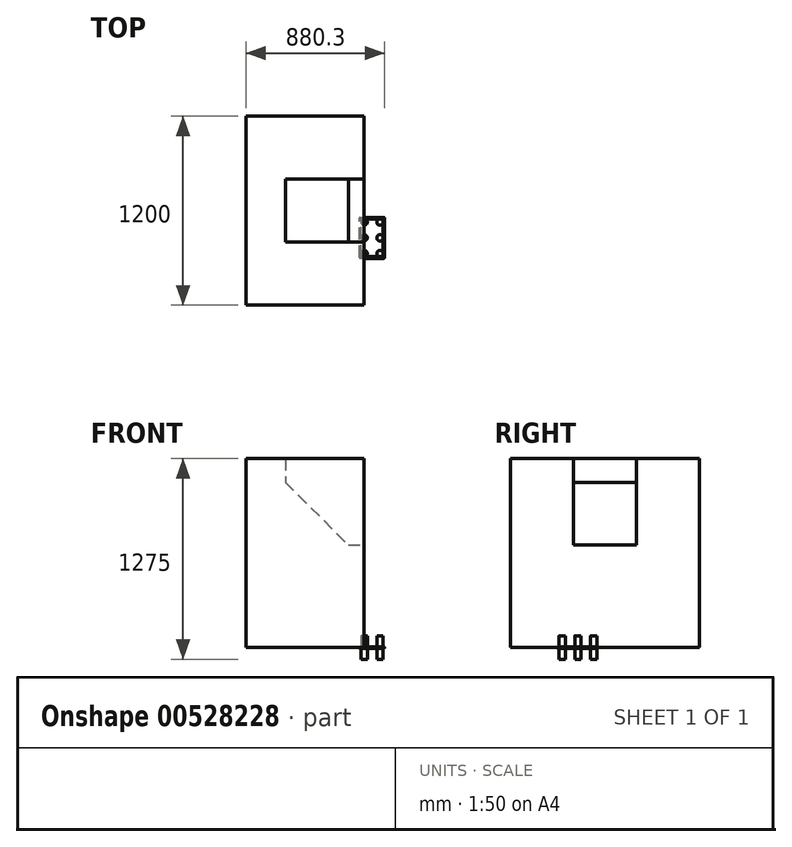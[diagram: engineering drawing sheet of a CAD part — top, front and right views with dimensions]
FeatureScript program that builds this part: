
annotation { "Feature Type Name" : "Feature", "Feature Type Description" : "" }
export const myFeature = defineFeature(function(context is Context, id is Id, definition is map)
    precondition{}
    {
        {
            var Q0;
            Q0=qCreatedBy(makeId("Front.planeOp"),FACE);
            var sketch = newSketch(context, id + "F0", { "sketchPlane" : qUnion([Q0])});
            skLineSegment(sketch, "E0.bottom", {"start": v(-750, 1200) * mm, "end": v(0, 1200) * mm});
            skLineSegment(sketch, "E0.top", {"start": v(-750, 0) * mm, "end": v(0, 0) * mm});
            skLineSegment(sketch, "E0.left", {"start": v(-750, 1200) * mm, "end": v(-750, 0) * mm});
            skLineSegment(sketch, "E0.right", {"start": v(0, 1200) * mm, "end": v(0, 0) * mm});
            skSolve(sketch);
        }
        {
            var Q0;
            Q0=makeQuery(id+"F0.imprint","IMPRINT",FACE,{"disambiguationData":[TD([[makeQuery(id+"F0.imprint","IMPRINT",EDGE,{"derivedFrom":sQuery(id+"F0.wireOp",EDGE,"E0.bottom")}),-1.0]])]});
            extrude(context, id + "F1", {"entities" : qUnion([Q0]), "endBound" : BoundingType.SYMMETRIC, "depth" : 1200 * mm, "offsetDistance" : 25 * mm});
        }
        {
            var Q0;
            Q0=qCreatedBy(makeId("Front.planeOp"),FACE);
            var sketch = newSketch(context, id + "F2", { "sketchPlane" : qUnion([Q0])});
            skLineSegment(sketch, "E1", {"start": v(0, 1200) * mm, "end": v(-500, 1200) * mm});
            skLineSegment(sketch, "E2", {"start": v(-500, 1200) * mm, "end": v(-500, 1050) * mm});
            skLineSegment(sketch, "E3", {"start": v(-100, 650) * mm, "end": v(0, 650) * mm});
            skLineSegment(sketch, "E4", {"start": v(0, 650) * mm, "end": v(0, 1200) * mm});
            skLineSegment(sketch, "E5", {"start": v(-500, 1050) * mm, "end": v(-100, 650) * mm});
            skSolve(sketch);
        }
        {
            var Q0;
            Q0 = qSketchRegion(id + "F2", true);
            extrude(context, id + "F3", {"entities" : qUnion([Q0]), "operationType" : NewBodyOperationType.REMOVE, "endBound" : BoundingType.SYMMETRIC, "oppositeDirection" : true, "depth" : 400 * mm, "offsetDistance" : 25 * mm});
        }
        {
            var Q0;
            Q0=makeQuery(id+"F3.boolean.opBoolean","COPY",FACE,{"derivedFrom":makeQuery(id+"F3.opExtrude","SWEPT_FACE",FACE,{"disambiguationData":[OSD([sQuery(id+"F2.wireOp",EDGE,"E5")])]})});
            var sketch = newSketch(context, id + "F4", { "sketchPlane" : qUnion([Q0])});
            skPoint(sketch, "E6", {"position": v(-813.17, 0) * mm});
            skCircle(sketch, "E7", {"center": v(-813.17, 0) * mm, "radius": 100 * mm});
            skSolve(sketch);
        }
        {
            var Q0;
            Q0=makeQuery(id+"F4.imprint","IMPRINT",FACE,{"disambiguationData":[TD([[makeQuery(id+"F4.imprint","IMPRINT",EDGE,{"derivedFrom":sQuery(id+"F4.wireOp",EDGE,"E7")}),1.0]])]});
            extrude(context, id + "F5", {"entities" : qUnion([Q0]), "operationType" : NewBodyOperationType.REMOVE, "endBound" : BoundingType.THROUGH_ALL, "oppositeDirection" : true, "depth" : 25 * mm, "offsetDistance" : 25 * mm});
        }
        {
            var Q0;
            Q0=qCreatedBy(makeId("Top.planeOp"),FACE);
            var sketch = newSketch(context, id + "F6", { "sketchPlane" : qUnion([Q0])});
            skLineSegment(sketch, "E8.bottom", {"start": v(-29.7, -42.66) * mm, "end": v(130.3, -42.66) * mm});
            skLineSegment(sketch, "E8.top", {"start": v(-29.7, -302.66) * mm, "end": v(130.3, -302.66) * mm});
            skLineSegment(sketch, "E8.left", {"start": v(-29.7, -42.66) * mm, "end": v(-29.7, -302.66) * mm});
            skLineSegment(sketch, "E8.right", {"start": v(130.3, -42.66) * mm, "end": v(130.3, -302.66) * mm});
            skLineSegment(sketch, "E9.0", {"start": v(-19.7, -52.66) * mm, "end": v(120.3, -52.66) * mm});
            skLineSegment(sketch, "E9.1", {"start": v(-19.7, -52.66) * mm, "end": v(-19.7, -292.66) * mm});
            skLineSegment(sketch, "E9.2", {"start": v(-19.7, -292.66) * mm, "end": v(120.3, -292.66) * mm});
            skLineSegment(sketch, "E9.3", {"start": v(120.3, -52.66) * mm, "end": v(120.3, -292.66) * mm});
            skPoint(sketch, "E10", {"position": v(100.3, -72.66) * mm});
            skPoint(sketch, "E11", {"position": v(0.3, -72.66) * mm});
            skPoint(sketch, "E12", {"position": v(0.3, -172.66) * mm});
            skPoint(sketch, "E13", {"position": v(100.3, -172.66) * mm});
            skPoint(sketch, "E14", {"position": v(0.3, -272.66) * mm});
            skPoint(sketch, "E15", {"position": v(100.3, -272.66) * mm});
            skCircle(sketch, "E16", {"center": v(0.3, -72.66) * mm, "radius": 20 * mm});
            skCircle(sketch, "E17", {"center": v(100.3, -72.66) * mm, "radius": 20 * mm});
            skCircle(sketch, "E18", {"center": v(100.3, -172.66) * mm, "radius": 20 * mm});
            skCircle(sketch, "E19", {"center": v(0.3, -172.66) * mm, "radius": 20 * mm});
            skCircle(sketch, "E20", {"center": v(100.3, -272.66) * mm, "radius": 20 * mm});
            skCircle(sketch, "E21", {"center": v(0.3, -272.66) * mm, "radius": 20 * mm});
            skSolve(sketch);
        }
        {
            var Q0;
            Q0=makeQuery(id+"F6.imprint","IMPRINT",FACE,{"disambiguationData":[TD([[makeQuery(id+"F6.imprint","IMPRINT",EDGE,{"derivedFrom":sQuery(id+"F6.wireOp",EDGE,"E19")}),1.0]])]});
            var Q1;
            Q1=makeQuery(id+"F6.imprint","IMPRINT",FACE,{"disambiguationData":[TD([[makeQuery(id+"F6.imprint","IMPRINT",EDGE,{"derivedFrom":sQuery(id+"F6.wireOp",EDGE,"E18")}),1.0]])]});
            var Q2;
            {var subQ0=sQuery(id+"F6.wireOp",EDGE,"E17");var subQ1=makeQuery(id+"F6.imprint","INTERSECT",VERTEX,{"derivedFrom":[sQuery(id+"F6.wireOp",EDGE,"E9.0"),subQ0]});Q2=makeQuery(id+"F6.imprint","IMPRINT",FACE,{"disambiguationData":[TD([[makeQuery(id+"F6.imprint","IMPRINT",EDGE,{"disambiguationData":[TD([[subQ1,1.0]])],"derivedFrom":subQ0}),1.0]])]});}
            var Q3;
            {var subQ0=sQuery(id+"F6.wireOp",EDGE,"E16");var subQ1=makeQuery(id+"F6.imprint","INTERSECT",VERTEX,{"derivedFrom":[sQuery(id+"F6.wireOp",EDGE,"E9.0"),subQ0]});Q3=makeQuery(id+"F6.imprint","IMPRINT",FACE,{"disambiguationData":[TD([[makeQuery(id+"F6.imprint","IMPRINT",EDGE,{"disambiguationData":[TD([[subQ1,-1.0]])],"derivedFrom":subQ0}),1.0]])]});}
            var Q4;
            {var subQ0=sQuery(id+"F6.wireOp",EDGE,"E21");var subQ1=makeQuery(id+"F6.imprint","INTERSECT",VERTEX,{"derivedFrom":[sQuery(id+"F6.wireOp",EDGE,"E9.1"),subQ0]});Q4=makeQuery(id+"F6.imprint","IMPRINT",FACE,{"disambiguationData":[TD([[makeQuery(id+"F6.imprint","IMPRINT",EDGE,{"disambiguationData":[TD([[subQ1,-1.0]])],"derivedFrom":subQ0}),1.0]])]});}
            var Q5;
            {var subQ0=sQuery(id+"F6.wireOp",EDGE,"E20");var subQ1=makeQuery(id+"F6.imprint","INTERSECT",VERTEX,{"derivedFrom":[sQuery(id+"F6.wireOp",EDGE,"E9.2"),subQ0]});Q5=makeQuery(id+"F6.imprint","IMPRINT",FACE,{"disambiguationData":[TD([[makeQuery(id+"F6.imprint","IMPRINT",EDGE,{"disambiguationData":[TD([[subQ1,1.0]])],"derivedFrom":subQ0}),1.0]])]});}
            extrude(context, id + "F7", {"entities" : qUnion([Q0, Q1, Q2, Q3, Q4, Q5]), "endBound" : BoundingType.SYMMETRIC, "depth" : 150 * mm, "offsetDistance" : 25 * mm});
        }
        {
            var Q0;
            Q0=makeQuery(id+"F6.imprint","IMPRINT",FACE,{"disambiguationData":[TD([[makeQuery(id+"F6.imprint","IMPRINT",EDGE,{"derivedFrom":sQuery(id+"F6.wireOp",EDGE,"E8.bottom")}),-1.0]])]});
            extrude(context, id + "F8", {"entities" : qUnion([Q0]), "endBound" : BoundingType.SYMMETRIC, "depth" : 10 * mm, "offsetDistance" : 25 * mm});
        }
        {
            var Q0;
            Q0=makeQuery(id+"F8.opExtrude","CAP_EDGE",EDGE,{"disambiguationData":[OSD([sQuery(id+"F6.wireOp",EDGE,"E8.left")])],"isStart":false});
            var Q1;
            Q1=makeQuery(id+"F8.opExtrude","CAP_EDGE",EDGE,{"disambiguationData":[OSD([sQuery(id+"F6.wireOp",EDGE,"E9.1")])],"isStart":false});
            var Q2;
            Q2=makeQuery(id+"F8.opExtrude","CAP_EDGE",EDGE,{"disambiguationData":[OSD([sQuery(id+"F6.wireOp",EDGE,"E8.left")])],"isStart":true});
            var Q3;
            Q3=makeQuery(id+"F8.opExtrude","CAP_EDGE",EDGE,{"disambiguationData":[OSD([sQuery(id+"F6.wireOp",EDGE,"E8.top")])],"isStart":true});
            var Q4;
            Q4=makeQuery(id+"F8.opExtrude","CAP_EDGE",EDGE,{"disambiguationData":[OSD([sQuery(id+"F6.wireOp",EDGE,"E8.top")])],"isStart":false});
            var Q5;
            Q5=makeQuery(id+"F8.opExtrude","CAP_EDGE",EDGE,{"disambiguationData":[OSD([sQuery(id+"F6.wireOp",EDGE,"E9.2")])],"isStart":false});
            var Q6;
            Q6=makeQuery(id+"F8.opExtrude","CAP_EDGE",EDGE,{"disambiguationData":[OSD([sQuery(id+"F6.wireOp",EDGE,"E9.2")])],"isStart":true});
            var Q7;
            Q7=makeQuery(id+"F8.opExtrude","CAP_EDGE",EDGE,{"disambiguationData":[OSD([sQuery(id+"F6.wireOp",EDGE,"E9.1")])],"isStart":true});
            var Q8;
            Q8=makeQuery(id+"F8.opExtrude","CAP_EDGE",EDGE,{"disambiguationData":[OSD([sQuery(id+"F6.wireOp",EDGE,"E9.3")])],"isStart":true});
            var Q9;
            Q9=makeQuery(id+"F8.opExtrude","CAP_EDGE",EDGE,{"disambiguationData":[OSD([sQuery(id+"F6.wireOp",EDGE,"E8.right")])],"isStart":true});
            var Q10;
            Q10=makeQuery(id+"F8.opExtrude","CAP_EDGE",EDGE,{"disambiguationData":[OSD([sQuery(id+"F6.wireOp",EDGE,"E8.right")])],"isStart":false});
            var Q11;
            Q11=makeQuery(id+"F8.opExtrude","CAP_EDGE",EDGE,{"disambiguationData":[OSD([sQuery(id+"F6.wireOp",EDGE,"E9.3")])],"isStart":false});
            var Q12;
            Q12=makeQuery(id+"F8.opExtrude","SWEPT_EDGE",EDGE,{"disambiguationData":[OSD([sQuery(id+"F6.wireOp",EDGE,"E8.top"),sQuery(id+"F6.wireOp",EDGE,"E8.right")])]});
            var Q13;
            Q13=makeQuery(id+"F8.opExtrude","SWEPT_EDGE",EDGE,{"disambiguationData":[OSD([sQuery(id+"F6.wireOp",EDGE,"E8.top"),sQuery(id+"F6.wireOp",EDGE,"E8.left")])]});
            var Q14;
            Q14=makeQuery(id+"F8.opExtrude","CAP_EDGE",EDGE,{"disambiguationData":[OSD([sQuery(id+"F6.wireOp",EDGE,"E8.bottom")])],"isStart":false});
            var Q15;
            Q15=makeQuery(id+"F8.opExtrude","CAP_EDGE",EDGE,{"disambiguationData":[OSD([sQuery(id+"F6.wireOp",EDGE,"E8.bottom")])],"isStart":true});
            var Q16;
            Q16=makeQuery(id+"F8.opExtrude","SWEPT_EDGE",EDGE,{"disambiguationData":[OSD([sQuery(id+"F6.wireOp",EDGE,"E8.bottom"),sQuery(id+"F6.wireOp",EDGE,"E8.right")])]});
            var Q17;
            Q17=makeQuery(id+"F8.opExtrude","CAP_EDGE",EDGE,{"disambiguationData":[OSD([sQuery(id+"F6.wireOp",EDGE,"E9.0")])],"isStart":false});
            var Q18;
            Q18=makeQuery(id+"F8.opExtrude","SWEPT_EDGE",EDGE,{"disambiguationData":[OSD([sQuery(id+"F6.wireOp",EDGE,"E8.bottom"),sQuery(id+"F6.wireOp",EDGE,"E8.left")])]});
            var Q19;
            Q19=makeQuery(id+"F8.opExtrude","CAP_EDGE",EDGE,{"disambiguationData":[OSD([sQuery(id+"F6.wireOp",EDGE,"E9.0")])],"isStart":true});
            fillet(context, id + "F9", {"entities" : qUnion([Q0, Q1, Q2, Q3, Q4, Q5, Q6, Q7, Q8, Q9, Q10, Q11, Q12, Q13, Q14, Q15, Q16, Q17, Q18, Q19]), "radius" : 5 * mm, "tangentPropagation" : true, "allowEdgeOverflow" : false});
        }
    });
